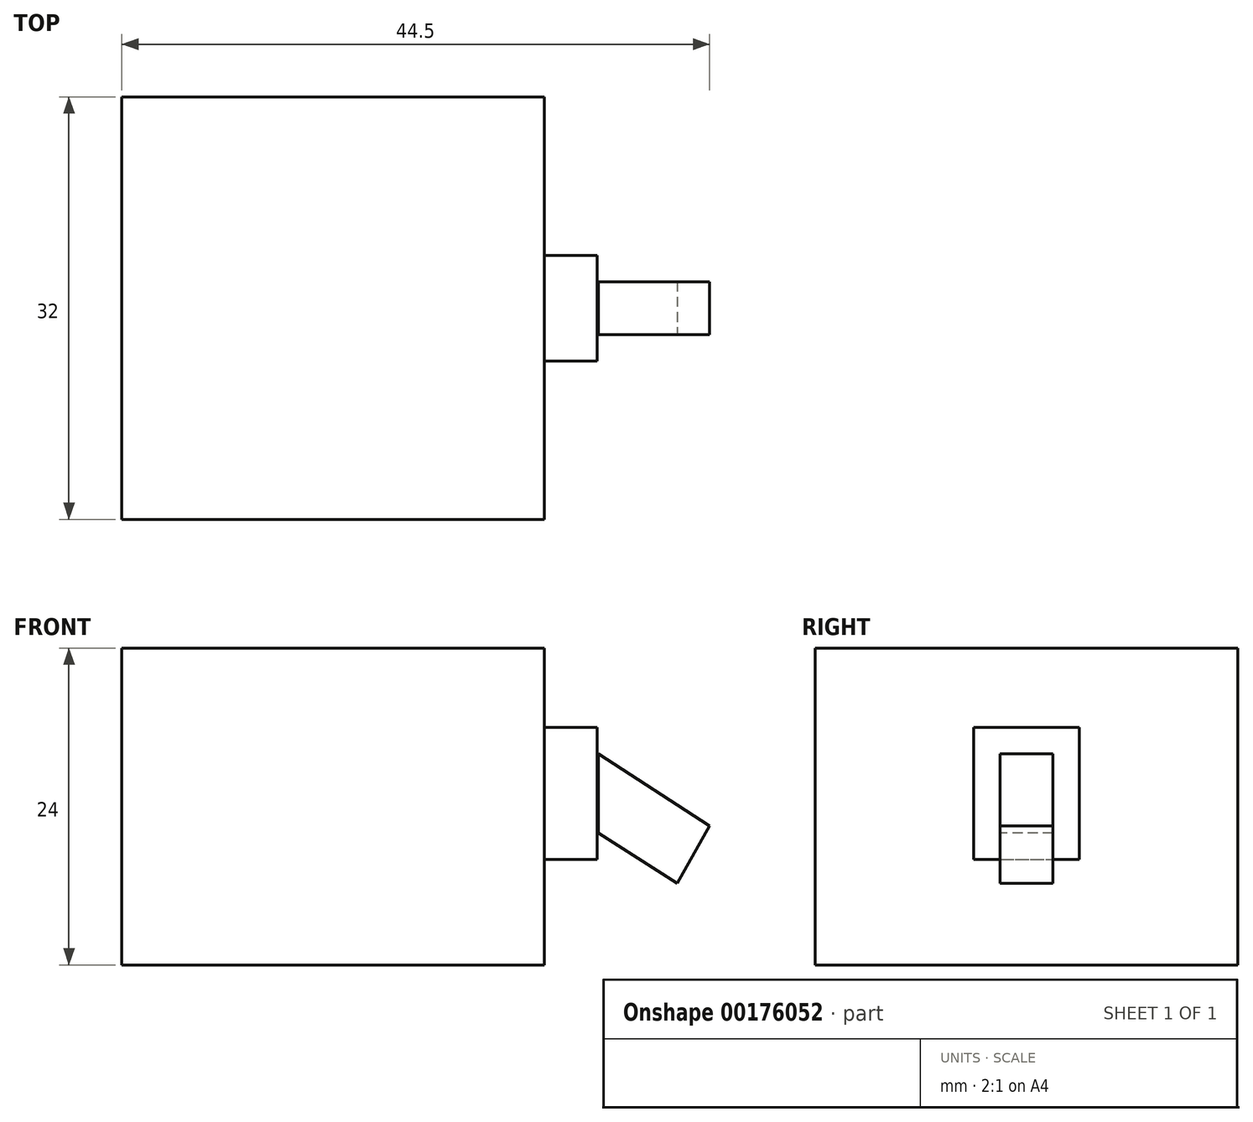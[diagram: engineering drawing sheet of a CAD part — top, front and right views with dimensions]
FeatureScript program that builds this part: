
annotation { "Feature Type Name" : "Feature", "Feature Type Description" : "" }
export const myFeature = defineFeature(function(context is Context, id is Id, definition is map)
    precondition{}
    {
        {
            var Q0;
            Q0=qCreatedBy(makeId("Right.planeOp"),FACE);
            var sketch = newSketch(context, id + "F0", { "sketchPlane" : qUnion([Q0])});
            skLineSegment(sketch, "E0.bottom", {"start": v(-16, 12) * mm, "end": v(16, 12) * mm});
            skLineSegment(sketch, "E0.top", {"start": v(-16, -12) * mm, "end": v(16, -12) * mm});
            skLineSegment(sketch, "E0.left", {"start": v(-16, 12) * mm, "end": v(-16, -12) * mm});
            skLineSegment(sketch, "E0.right", {"start": v(16, 12) * mm, "end": v(16, -12) * mm});
            skPoint(sketch, "E0.middle", {"position": v(0, 0) * mm});
            skSolve(sketch);
        }
        {
            var Q0;
            Q0 = qSketchRegion(id + "F0", true);
            extrude(context, id + "F1", {"entities" : qUnion([Q0]), "depth" : 32 * mm});
        }
        {
            var Q0;
            Q0=makeQuery(id+"F1.opExtrude","CAP_FACE",FACE,{"disambiguationData":[OSD([sQuery(id+"F0.wireOp",EDGE,"E0.bottom"),sQuery(id+"F0.wireOp",EDGE,"E0.top"),sQuery(id+"F0.wireOp",EDGE,"E0.left"),sQuery(id+"F0.wireOp",EDGE,"E0.right")])],"isStart":false});
            var sketch = newSketch(context, id + "F2", { "sketchPlane" : qUnion([Q0])});
            skLineSegment(sketch, "E1", {"start": v(-4, -4) * mm, "end": v(4, -4) * mm});
            skLineSegment(sketch, "E2", {"start": v(4, -4) * mm, "end": v(4, 6) * mm});
            skLineSegment(sketch, "E3", {"start": v(4, 6) * mm, "end": v(-4, 6) * mm});
            skLineSegment(sketch, "E4", {"start": v(-4, -4) * mm, "end": v(-4, 6) * mm});
            skPoint(sketch, "E5.end.orphan", {"position": v(-16, -4) * mm});
            skSolve(sketch);
        }
        {
            var Q0;
            Q0 = qSketchRegion(id + "F2", true);
            extrude(context, id + "F3", {"entities" : qUnion([Q0]), "depth" : 4 * mm});
        }
        {
            var Q0;
            Q0=makeQuery(id+"F3.opExtrude","CAP_FACE",FACE,{"disambiguationData":[OSD([sQuery(id+"F2.wireOp",EDGE,"E1"),sQuery(id+"F2.wireOp",EDGE,"E2"),sQuery(id+"F2.wireOp",EDGE,"E3"),sQuery(id+"F2.wireOp",EDGE,"E4")])],"isStart":false});
            var sketch = newSketch(context, id + "F4", { "sketchPlane" : qUnion([Q0])});
            skLineSegment(sketch, "E6", {"start": v(2, 4) * mm, "end": v(2, -2) * mm});
            skLineSegment(sketch, "E7", {"start": v(2, -2) * mm, "end": v(-2, -2) * mm});
            skLineSegment(sketch, "E8", {"start": v(-2, -2) * mm, "end": v(-2, 4) * mm});
            skLineSegment(sketch, "E9", {"start": v(-2, 4) * mm, "end": v(2, 4) * mm});
            skSolve(sketch);
        }
        {
            var Q0;
            Q0 = qSketchRegion(id + "F4", true);
            extrude(context, id + "F5", {"entities" : qUnion([Q0]), "operationType" : NewBodyOperationType.ADD, "depth" : 0.1 * mm});
        }
        {
            var Q0;
            Q0=makeQuery(id+"F5.opExtrude","SWEPT_FACE",FACE,{"disambiguationData":[OSD([sQuery(id+"F4.wireOp",EDGE,"E8")])]});
            var sketch = newSketch(context, id + "F6", { "sketchPlane" : qUnion([Q0])});
            skLineSegment(sketch, "E10", {"start": v(36.1, 4) * mm, "end": v(44.5, -1.47) * mm});
            skLineSegment(sketch, "E11", {"start": v(36.1, -2) * mm, "end": v(42.05, -5.83) * mm});
            skLineSegment(sketch, "E12", {"start": v(44.5, -1.47) * mm, "end": v(42.05, -5.83) * mm});
            skLineSegment(sketch, "E13", {"start": v(36.1, 4) * mm, "end": v(36.1, -2) * mm});
            skSolve(sketch);
        }
        {
            var Q0;
            Q0 = qSketchRegion(id + "F6", true);
            extrude(context, id + "F7", {"entities" : qUnion([Q0]), "oppositeDirection" : true, "depth" : 4 * mm});
        }
    });
